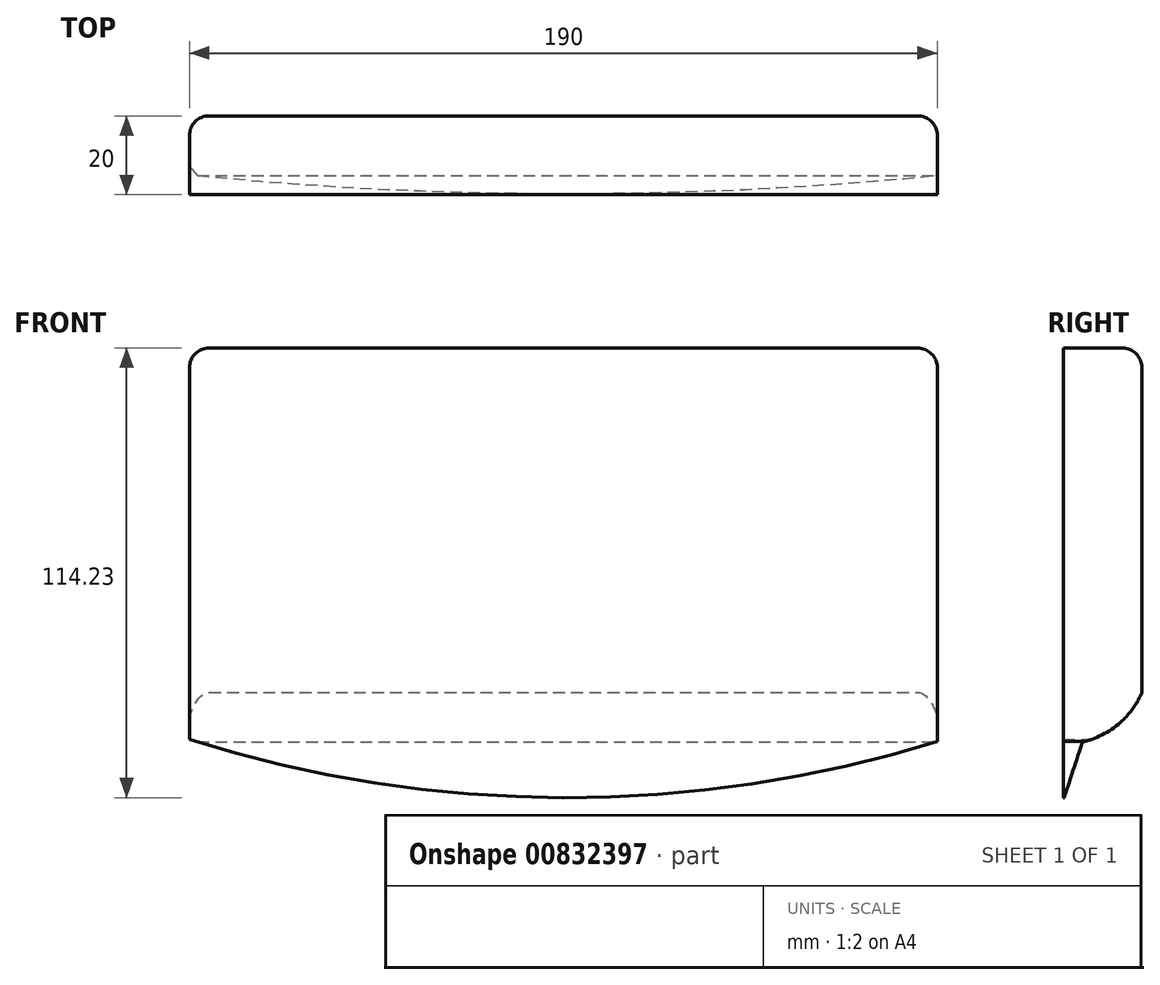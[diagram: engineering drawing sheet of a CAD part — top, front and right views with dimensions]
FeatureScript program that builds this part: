
annotation { "Feature Type Name" : "Feature", "Feature Type Description" : "" }
export const myFeature = defineFeature(function(context is Context, id is Id, definition is map)
    precondition{}
    {
        {
            var Q0;
            Q0=qCreatedBy(makeId("Front.planeOp"),FACE);
            var sketch = newSketch(context, id + "F0", { "sketchPlane" : qUnion([Q0])});
            skLineSegment(sketch, "E0", {"start": v(-98.97, 28.54) * mm, "end": v(91.03, 28.54) * mm});
            skLineSegment(sketch, "E1", {"start": v(91.03, 28.54) * mm, "end": v(91.03, -71.46) * mm});
            skLineSegment(sketch, "E2", {"start": v(-98.97, 28.54) * mm, "end": v(-98.97, -70.92) * mm});
            skArc(sketch, "E3", {"start": v(-98.97, -70.92) * mm, "mid": v(-4, -85.69) * mm, "end": v(91.03, -71.46) * mm});
            skSolve(sketch);
        }
        {
            var Q0;
            Q0=makeQuery(id+"F0.imprint","IMPRINT",FACE,{"disambiguationData":[TD([[makeQuery(id+"F0.imprint","IMPRINT",EDGE,{"derivedFrom":sQuery(id+"F0.wireOp",EDGE,"E0")}),-1.0]])]});
            extrude(context, id + "F1", {"entities" : qUnion([Q0]), "depth" : 20 * mm, "offsetDistance" : 25 * mm});
        }
        {
            var Q0;
            Q0=qCreatedBy(makeId("Right.planeOp"),FACE);
            var sketch = newSketch(context, id + "F2", { "sketchPlane" : qUnion([Q0])});
            skArc(sketch, "E4", {"start": v(-15.14, -71.56) * mm, "mid": v(-0.6, -60.21) * mm, "end": v(0, -41.78) * mm});
            skLineSegment(sketch, "E5", {"start": v(-15.14, -71.56) * mm, "end": v(-19.82, -85.88) * mm});
            skLineSegment(sketch, "E6", {"start": v(-19.82, -85.88) * mm, "end": v(-19.82, -85.88) * mm});
            skLineSegment(sketch, "E7", {"start": v(3.4, -87.58) * mm, "end": v(-19.82, -85.88) * mm});
            skLineSegment(sketch, "E8", {"start": v(3.4, -87.58) * mm, "end": v(10.87, -61.35) * mm});
            skLineSegment(sketch, "E9", {"start": v(13.54, -62.14) * mm, "end": v(13.54, -62.14) * mm});
            skLineSegment(sketch, "E10", {"start": v(10.87, -61.35) * mm, "end": v(0, -41.78) * mm});
            skSolve(sketch);
        }
        {
            var Q0;
            Q0=makeQuery(id+"F2.imprint","IMPRINT",FACE,{"disambiguationData":[TD([[makeQuery(id+"F2.imprint","IMPRINT",EDGE,{"derivedFrom":sQuery(id+"F2.wireOp",EDGE,"E4")}),-1.0]])]});
            extrude(context, id + "F3", {"entities" : qUnion([Q0]), "operationType" : NewBodyOperationType.REMOVE, "endBound" : BoundingType.SYMMETRIC, "oppositeDirection" : true, "depth" : 200 * mm, "offsetDistance" : 25 * mm});
        }
        {
            var Q0;
            Q0=makeQuery(id+"F1.opExtrude","SWEPT_EDGE",EDGE,{"disambiguationData":[OSD([sQuery(id+"F0.wireOp",EDGE,"E0"),sQuery(id+"F0.wireOp",EDGE,"E1")])]});
            var Q1;
            Q1=makeQuery(id+"F1.opExtrude","CAP_EDGE",EDGE,{"disambiguationData":[OSD([sQuery(id+"F0.wireOp",EDGE,"E0")])],"isStart":true});
            var Q2;
            Q2=makeQuery(id+"F1.opExtrude","CAP_EDGE",EDGE,{"disambiguationData":[OSD([sQuery(id+"F0.wireOp",EDGE,"E2")])],"isStart":true});
            var Q3;
            Q3=makeQuery(id+"F1.opExtrude","SWEPT_EDGE",EDGE,{"disambiguationData":[OSD([sQuery(id+"F0.wireOp",EDGE,"E0"),sQuery(id+"F0.wireOp",EDGE,"E2")])]});
            var Q4;
            Q4=makeQuery(id+"F1.opExtrude","CAP_EDGE",EDGE,{"disambiguationData":[OSD([sQuery(id+"F0.wireOp",EDGE,"E1")])],"isStart":true});
            fillet(context, id + "F4", {"entities" : qUnion([Q0, Q1, Q2, Q3, Q4]), "radius" : 5 * mm, "tangentPropagation" : true, "allowEdgeOverflow" : false});
        }
    });
